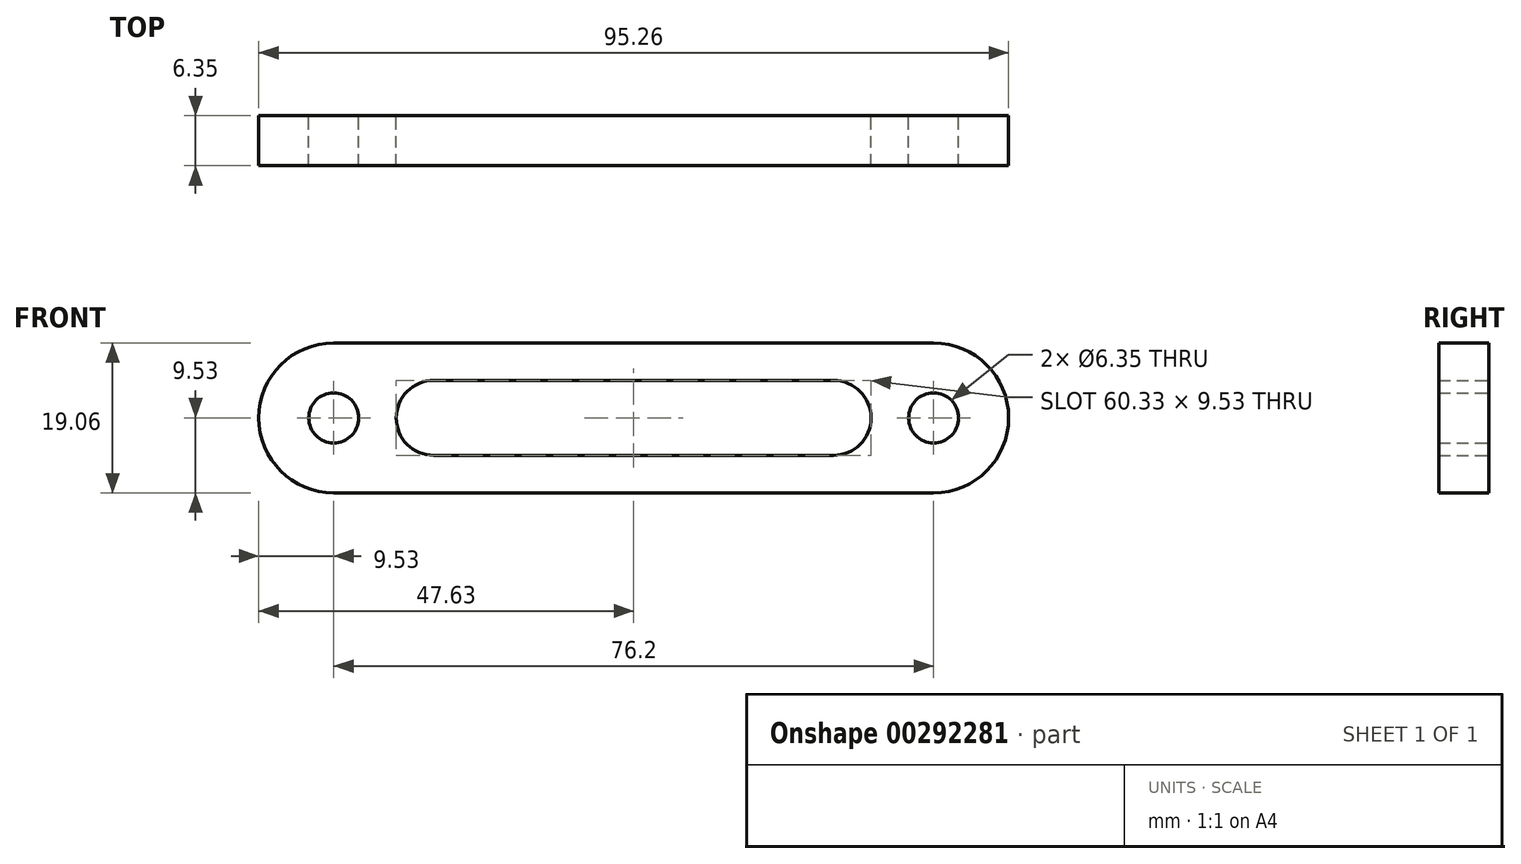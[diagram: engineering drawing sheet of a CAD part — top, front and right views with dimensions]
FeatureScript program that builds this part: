
annotation { "Feature Type Name" : "Feature", "Feature Type Description" : "" }
export const myFeature = defineFeature(function(context is Context, id is Id, definition is map)
    precondition{}
    {
        {
            var Q0;
            Q0=qCreatedBy(makeId("Front.planeOp"),FACE);
            var sketch = newSketch(context, id + "F0", { "sketchPlane" : qUnion([Q0])});
            skCircle(sketch, "E0", {"center": v(0, 0) * mm, "radius": 3.18 * mm});
            skArc(sketch, "E1", {"start": v(0, 9.53) * mm, "mid": v(-9.53, 0) * mm, "end": v(0, -9.53) * mm});
            skArc(sketch, "E2", {"start": v(12.7, 4.76) * mm, "mid": v(7.94, 0) * mm, "end": v(12.7, -4.76) * mm});
            skCircle(sketch, "E3.MirrorC", {"center": v(76.2, 0) * mm, "radius": 3.18 * mm});
            skArc(sketch, "E4.MirrorC", {"start": v(76.2, 9.53) * mm, "mid": v(85.73, 0) * mm, "end": v(76.2, -9.53) * mm});
            skArc(sketch, "E5.MirrorC", {"start": v(63.5, 4.76) * mm, "mid": v(68.26, 0) * mm, "end": v(63.5, -4.76) * mm});
            skLineSegment(sketch, "E6", {"start": v(0, 9.53) * mm, "end": v(76.2, 9.52) * mm});
            skLineSegment(sketch, "E7", {"start": v(76.2, -9.52) * mm, "end": v(0, -9.53) * mm});
            skLineSegment(sketch, "E8", {"start": v(12.7, -4.76) * mm, "end": v(63.5, -4.76) * mm});
            skLineSegment(sketch, "E9", {"start": v(63.5, 4.76) * mm, "end": v(12.7, 4.76) * mm});
            skSolve(sketch);
        }
        {
            var Q0;
            Q0=makeQuery(id+"F0.imprint","IMPRINT",FACE,{"disambiguationData":[TD([[makeQuery(id+"F0.imprint","IMPRINT",EDGE,{"derivedFrom":sQuery(id+"F0.wireOp",EDGE,"E0")}),-1.0]])]});
            extrude(context, id + "F1", {"entities" : qUnion([Q0]), "depth" : 6.35 * mm});
        }
    });
